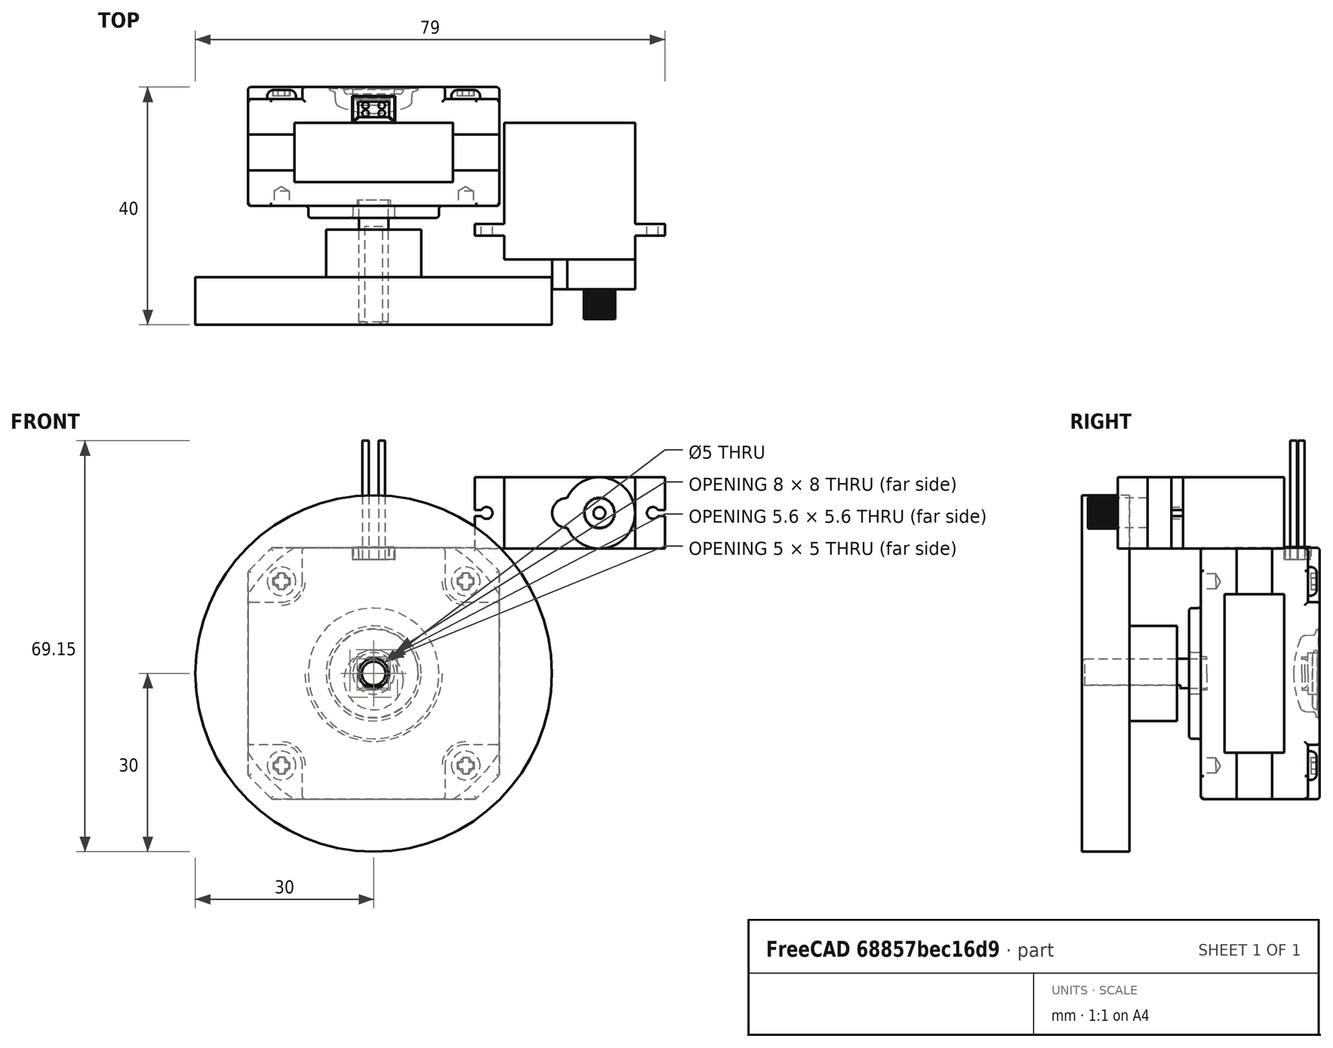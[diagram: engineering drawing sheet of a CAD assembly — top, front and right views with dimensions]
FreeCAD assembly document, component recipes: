
FREECAD ASSEMBLY — COMPONENT RECIPES ("proto-01")

This assembly document has 2 components, labeled P0..P1 below (a component is one placed body or linked part). 2 of them carry a construction recipe — the FreeCAD feature program that regenerates the part from scratch, quoted from this document or its linked companion documents; the rest are supplied as boundary geometry only. No exploded tour is included for this assembly.
COMPONENT P0 — recipe-attached ("EnsembleMoteurRoue-Droit", modeled in this document).
Construction recipe (the document's own serialized feature program — sketch geometry with constraints, then the solid features built on it; lengths are millimeters unless a unit is written):

FEATURE [Sketcher::SketchObject] Sketch
  ArcFitTolerance = 1e-06
  AttachmentSupport = -> [YZ_Plane001]
  ExternalBSplineMaxDegree = 5
  ExternalBSplineTolerance = 0.0001
  FixShape = 1
  FullyConstrained = true
  InternalTolerance = 1e-06
  InvalidShape = false
  MakeInternals = false
  MapMode = 5
  Placement = pos=(0,0,0) rot=(0.57735,0.57735,0.57735;2.0944rad)
  Support = -> [YZ_Plane001]
  TreeRank = 31
  ValidateShape = false
  sketch-geometry (9):
    g0: LineSegment StartX=0 StartY=0 StartZ=0 EndX=8 EndY=0 EndZ=0
    g1: LineSegment [constr] StartX=8 StartY=0 StartZ=0 EndX=8 EndY=30 EndZ=0
    g2: LineSegment StartX=8 StartY=30 StartZ=0 EndX=0 EndY=30 EndZ=0
    g3: LineSegment StartX=0 StartY=30 StartZ=0 EndX=0 EndY=0 EndZ=0
    g4: LineSegment StartX=8 StartY=0 StartZ=0 EndX=16 EndY=0 EndZ=0
    g5: LineSegment StartX=16 StartY=0 StartZ=0 EndX=16 EndY=8 EndZ=0
    g6: LineSegment StartX=16 StartY=8 StartZ=0 EndX=8 EndY=8 EndZ=0
    g7: LineSegment [constr] StartX=8 StartY=8 StartZ=0 EndX=8 EndY=0 EndZ=0
    g8: LineSegment StartX=8 StartY=8 StartZ=0 EndX=8 EndY=30 EndZ=0
  constraints (24):
    c: Coincident(g0,g1)
    c: Coincident(g1,g2)
    c: Coincident(g2,g3)
    c: Coincident(g3,g0)
    c: Horizontal(g0)
    c: Horizontal(g2)
    c: Vertical(g1)
    c: Vertical(g3)
    c: Coincident(g0,g-1)
    c: Coincident(g4,g5)
    c: Coincident(g5,g6)
    c: Coincident(g6,g7)
    c: Coincident(g7,g4)
    c: Horizontal(g4)
    c: Horizontal(g6)
    c: Vertical(g5)
    c: Vertical(g7)
    c: Coincident(g4,g0)
    c: Coincident(g8,g6)
    c: Coincident(g8,g2)
    c: DistanceX(g0,g4) = 16
    c: DistanceY(g3,g3) = 30
    c: DistanceX(g2,g2) = 8
    c: DistanceY(g5,g5) = 8
FEATURE [PartDesign::Revolution] Revolution
  AddSubType = 0
  Angle = 360
  Axis = (3e-16,1,-2e-16)
  Base = (0,0,0)
  ClaimChildren = false
  Fit = 0
  FitJoin = 0
  FixShape = 1
  InnerFit = 0
  InnerFitJoin = 0
  InvalidShape = false
  Linearize = true
  NewSolid = false
  Profile = -> Sketch
  ReferenceAxis = -> Sketch [H_Axis]
  Refine = true
  Suppress = false
  TreeRank = 32
  ValidateShape = true
  _ProfileBasedVersion = 1
FEATURE [Sketcher::SketchObject] Sketch001
  ArcFitTolerance = 1e-06
  AttachmentSupport = -> [XZ_Plane001]
  ExternalBSplineMaxDegree = 5
  ExternalBSplineTolerance = 0.0001
  FixShape = 1
  FullyConstrained = true
  InternalTolerance = 1e-06
  InvalidShape = false
  MakeInternals = false
  MapMode = 5
  Placement = pos=(0,0,0) rot=(1,0,0;1.5708rad)
  Support = -> [XZ_Plane001]
  TreeRank = 33
  ValidateShape = false
  sketch-geometry (1):
    g0: Circle CenterX=0 CenterY=0 CenterZ=0 NormalX=0 NormalY=0 NormalZ=1 AngleXU=0 Radius=2.5
  constraints (2):
    c: Coincident(g0,g-1)
    c: Diameter(g0) = 5
FEATURE [PartDesign::Pocket] Pocket
  AddSubType = 1
  AlongSketchNormal = false
  AutoTaperInnerAngle = true
  BaseFeature = -> Revolution
  CheckUpToFaceLimits = true
  ClaimChildren = false
  Direction = (0,1,-2e-16)
  Fit = 0
  FitJoin = 0
  FixShape = 1
  InnerFit = 0
  InnerFitJoin = 0
  InvalidShape = false
  Length = 5
  Length2 = 10
  Linearize = true
  NewSolid = false
  Profile = -> Sketch001
  ReferenceAxis = -> Sketch001 [N_Axis]
  Refine = true
  Suppress = false
  TaperInnerAngle = 0
  TaperInnerAngleRev = 0
  TreeRank = 34
  Type = 1
  ValidateShape = true
  _ProfileBasedVersion = 1
  _Version = 1
FEATURE [PartDesign::Body] Body001  label="Roue60mm"
  AutoGroupSolids = false
  ClaimAllChildren = false
  ExportMode = 0
  FixShape = 1
  Group = -> [Sketch,Revolution,Sketch001,Pocket]
  InvalidShape = false
  Origin = -> Origin002
  Placement = pos=(0,-40,0) rot=(0,0,1;0rad)
  SingleSolid = true
  Tip = -> Pocket
  TreeRank = 27
  ValidateShape = false
  _ExportChildren = -> [Revolution,Pocket]
  _GroupVersion = 1
COMPONENT P1 — recipe-attached ("Eye", modeled in this document).
Construction recipe (the document's own serialized feature program — sketch geometry with constraints, then the solid features built on it; lengths are millimeters unless a unit is written):

FEATURE [Sketcher::SketchObject] Sketch104
  ArcFitTolerance = 1e-06
  AttachmentSupport = -> [YZ_Plane033]
  ExternalBSplineMaxDegree = 5
  ExternalBSplineTolerance = 0.0001
  FixShape = 1
  FullyConstrained = true
  InternalTolerance = 1e-06
  InvalidShape = false
  MakeInternals = false
  MapMode = 5
  Placement = pos=(0,0,0) rot=(0.57735,0.57735,0.57735;2.0944rad)
  Support = -> [YZ_Plane033]
  TreeRank = 943
  ValidateShape = false
  sketch-geometry (6):
    g0: LineSegment StartX=0 StartY=0 StartZ=0 EndX=0 EndY=7.5 EndZ=0
    g1: ArcOfCircle CenterX=10.8587 CenterY=0 CenterZ=0 NormalX=0 NormalY=0 NormalZ=1 AngleXU=0 Radius=15.2587 StartAngle=2.70988 EndAngle=3.14159
    g2: LineSegment StartX=-3 StartY=6.3847 StartZ=0 EndX=-0.8 EndY=6.5 EndZ=0
    g3: LineSegment StartX=-0.8 StartY=6.5 StartZ=0 EndX=-0.5 EndY=7.5 EndZ=0
    g4: LineSegment StartX=-0.5 StartY=7.5 StartZ=0 EndX=0 EndY=7.5 EndZ=0
    g5: LineSegment StartX=-4.4 StartY=0 StartZ=0 EndX=0 EndY=0 EndZ=0
  constraints (18):
    c: Coincident(g0,g-1)
    c: PointOnObject(g0,g-2)
    c: DistanceY(g0,g0) = 7.5
    c: PointOnObject(g1,g-1)
    c: PointOnObject(g1,g-1)
    c: Coincident(g2,g1)
    c: Coincident(g3,g2)
    c: Coincident(g4,g3)
    c: Coincident(g4,g0)
    c: Horizontal(g4)
    c: DistanceX(g4,g4) = 0.5
    c: DistanceX(g2,g0) = 0.8
    c: DistanceY(g0,g2) = 6.5
    c: Angle(g-1,g2) = 0.0523599
    c: DistanceX(g1,g0) = 4.4
    c: DistanceX(g1,g0) = 3
    c: Coincident(g5,g1)
    c: Coincident(g5,g0)
FEATURE [PartDesign::Revolution] Revolution005
  AddSubType = 0
  Angle = 360
  Axis = (3e-16,1,-2e-16)
  Base = (0,0,0)
  ClaimChildren = false
  Fit = 0
  FitJoin = 0
  FixShape = 1
  InnerFit = 0
  InnerFitJoin = 0
  InvalidShape = false
  Linearize = true
  NewSolid = false
  Profile = -> Sketch104
  ReferenceAxis = -> Sketch104 [H_Axis]
  Refine = true
  Suppress = false
  TreeRank = 944
  ValidateShape = false
  _ProfileBasedVersion = 1
FEATURE [PartDesign::Fillet] Fillet055
  AddSubType = 0
  Base = -> Revolution005 [Edge1]
  BaseFeature = -> Revolution005
  FixShape = 1
  InvalidShape = false
  NewSolid = false
  Radius = 1
  Refine = true
  SupportTransform = false
  Suppress = false
  TreeRank = 945
  UseAllEdges = false
  ValidateShape = false
FEATURE [PartDesign::Fillet] Fillet056
  AddSubType = 0
  Base = -> Fillet055 [Edge7]
  BaseFeature = -> Fillet055
  FixShape = 1
  InvalidShape = false
  NewSolid = false
  Radius = 0.4
  Refine = true
  SupportTransform = false
  Suppress = false
  TreeRank = 946
  UseAllEdges = false
  ValidateShape = false
FEATURE [PartDesign::Fillet] Fillet057
  AddSubType = 0
  Base = -> Fillet056 [Edge9]
  BaseFeature = -> Fillet056
  FixShape = 1
  InvalidShape = false
  NewSolid = false
  Radius = 0.4
  Refine = true
  SupportTransform = false
  Suppress = false
  TreeRank = 947
  UseAllEdges = false
  ValidateShape = false
FEATURE [PartDesign::Pocket] Pocket054
  AddSubType = 1
  AlongSketchNormal = false
  AutoTaperInnerAngle = true
  BaseFeature = -> Fillet057
  CheckUpToFaceLimits = true
  ClaimChildren = false
  Direction = (-3e-16,-1,2e-16)
  Fit = 0
  FitJoin = 0
  FixShape = 1
  InnerFit = 0
  InnerFitJoin = 0
  InvalidShape = false
  Length = 0.2
  Length2 = 10
  Linearize = true
  NewSolid = false
  Profile = -> Fillet057 [Face6]
  Refine = true
  Suppress = false
  TaperInnerAngle = 0
  TaperInnerAngleRev = 0
  TreeRank = 963
  Type = 0
  ValidateShape = false
  _ProfileBasedVersion = 1
  _Version = 1
FEATURE [PartDesign::Body] Body027  label="Transparent"
  AutoGroupSolids = false
  ClaimAllChildren = false
  ExportMode = 0
  FixShape = 1
  Group = -> [Sketch104,Revolution005,Fillet055,Fillet056,Fillet057,Pocket054]
  InvalidShape = false
  Origin = -> Origin039
  SingleSolid = true
  Tip = -> Pocket054
  TreeRank = 990
  ValidateShape = false
  _ExportChildren = -> [Revolution005,Fillet055,Fillet056,Fillet057,Pocket054]
  _GroupVersion = 1
FEATURE [Sketcher::SketchObject] Sketch105
  ArcFitTolerance = 1e-06
  AttachmentSupport = -> [XZ_Plane035]
  ExternalBSplineMaxDegree = 5
  ExternalBSplineTolerance = 0.0001
  FixShape = 1
  FullyConstrained = true
  InternalTolerance = 1e-06
  InvalidShape = false
  MakeInternals = false
  MapMode = 5
  Placement = pos=(0,0,0) rot=(1,0,0;1.5708rad)
  Support = -> [XZ_Plane035]
  TreeRank = 974
  ValidateShape = false
  sketch-geometry (1):
    g0: Circle CenterX=0 CenterY=0 CenterZ=0 NormalX=0 NormalY=0 NormalZ=1 AngleXU=0 Radius=7.5
  constraints (2):
    c: Coincident(g0,g-1)
    c: Diameter(g0) = 15
FEATURE [PartDesign::Pad] Pad043
  AddSubType = 0
  AlongSketchNormal = false
  AutoTaperInnerAngle = true
  CheckUpToFaceLimits = true
  ClaimChildren = false
  Direction = (0,-1,-2e-16)
  Fit = 0
  FitJoin = 0
  FixShape = 1
  InnerFit = 0
  InnerFitJoin = 0
  InvalidShape = false
  Length = 0.2
  Length2 = 10
  Linearize = true
  NewSolid = false
  Profile = -> Sketch105
  ReferenceAxis = -> Sketch105 [N_Axis]
  Refine = true
  Suppress = false
  TaperInnerAngle = 0
  TaperInnerAngleRev = 0
  TreeRank = 975
  Type = 0
  ValidateShape = false
  _ProfileBasedVersion = 1
FEATURE [PartDesign::Body] Body028  label="SupportColor"
  AutoGroupSolids = false
  ClaimAllChildren = false
  ExportMode = 0
  FixShape = 1
  Group = -> [Sketch105,Pad043]
  InvalidShape = false
  Origin = -> Origin041
  SingleSolid = true
  Tip = -> Pad043
  TreeRank = 991
  ValidateShape = false
  _ExportChildren = -> [Pad043]
  _GroupVersion = 1
FEATURE [Sketcher::SketchObject] Sketch106
  ArcFitTolerance = 1e-06
  AttachmentSupport = -> [XZ_Plane036]
  ExternalBSplineMaxDegree = 5
  ExternalBSplineTolerance = 0.0001
  FixShape = 1
  FullyConstrained = true
  InternalTolerance = 1e-06
  InvalidShape = false
  MakeInternals = false
  MapMode = 5
  Placement = pos=(0,0,0) rot=(1,0,0;1.5708rad)
  Support = -> [XZ_Plane036]
  TreeRank = 987
  ValidateShape = false
  sketch-geometry (1):
    g0: Circle CenterX=0 CenterY=-1.5 CenterZ=0 NormalX=0 NormalY=0 NormalZ=1 AngleXU=0 Radius=5
  constraints (3):
    c: PointOnObject(g0,g-2)
    c: Diameter(g0) = 10
    c: DistanceY(g0,g-1) = 1.5
FEATURE [PartDesign::Pad] Pad044
  AddSubType = 0
  AlongSketchNormal = false
  AutoTaperInnerAngle = true
  CheckUpToFaceLimits = true
  ClaimChildren = false
  Direction = (0,-1,-2e-16)
  Fit = 0
  FitJoin = 0
  FixShape = 1
  InnerFit = 0
  InnerFitJoin = 0
  InvalidShape = false
  Length = 0.8
  Length2 = 10
  Linearize = true
  NewSolid = false
  Profile = -> Sketch106
  ReferenceAxis = -> Sketch106 [N_Axis]
  Refine = true
  Suppress = false
  TaperInnerAngle = 0
  TaperInnerAngleRev = 0
  TreeRank = 988
  Type = 0
  ValidateShape = false
  _ProfileBasedVersion = 1
FEATURE [PartDesign::Fillet] Fillet058
  AddSubType = 0
  Base = -> Pad044 [Edge3]
  BaseFeature = -> Pad044
  FixShape = 1
  InvalidShape = false
  NewSolid = false
  Radius = 0.7
  Refine = true
  SupportTransform = false
  Suppress = false
  TreeRank = 989
  UseAllEdges = false
  ValidateShape = false
FEATURE [PartDesign::Body] Body029  label="Pupille"
  AutoGroupSolids = false
  ClaimAllChildren = false
  ExportMode = 0
  FixShape = 1
  Group = -> [Sketch106,Pad044,Fillet058]
  InvalidShape = false
  Origin = -> Origin042
  Placement = pos=(0,-0.4,0.4) rot=(0,0,1;0rad)
  SingleSolid = true
  Tip = -> Fillet058
  TreeRank = 992
  ValidateShape = false
  _ExportChildren = -> [Pad044,Fillet058]
  _GroupVersion = 1
PROVENANCE & LICENSES
A FreeCAD (.FCStd) document from a public repository crawl; recipes are the document's own serialized feature recipes (and, for linked parts, companion documents' recipes).
License: as declared in the source repository (recorded in the dataset sidecar).
